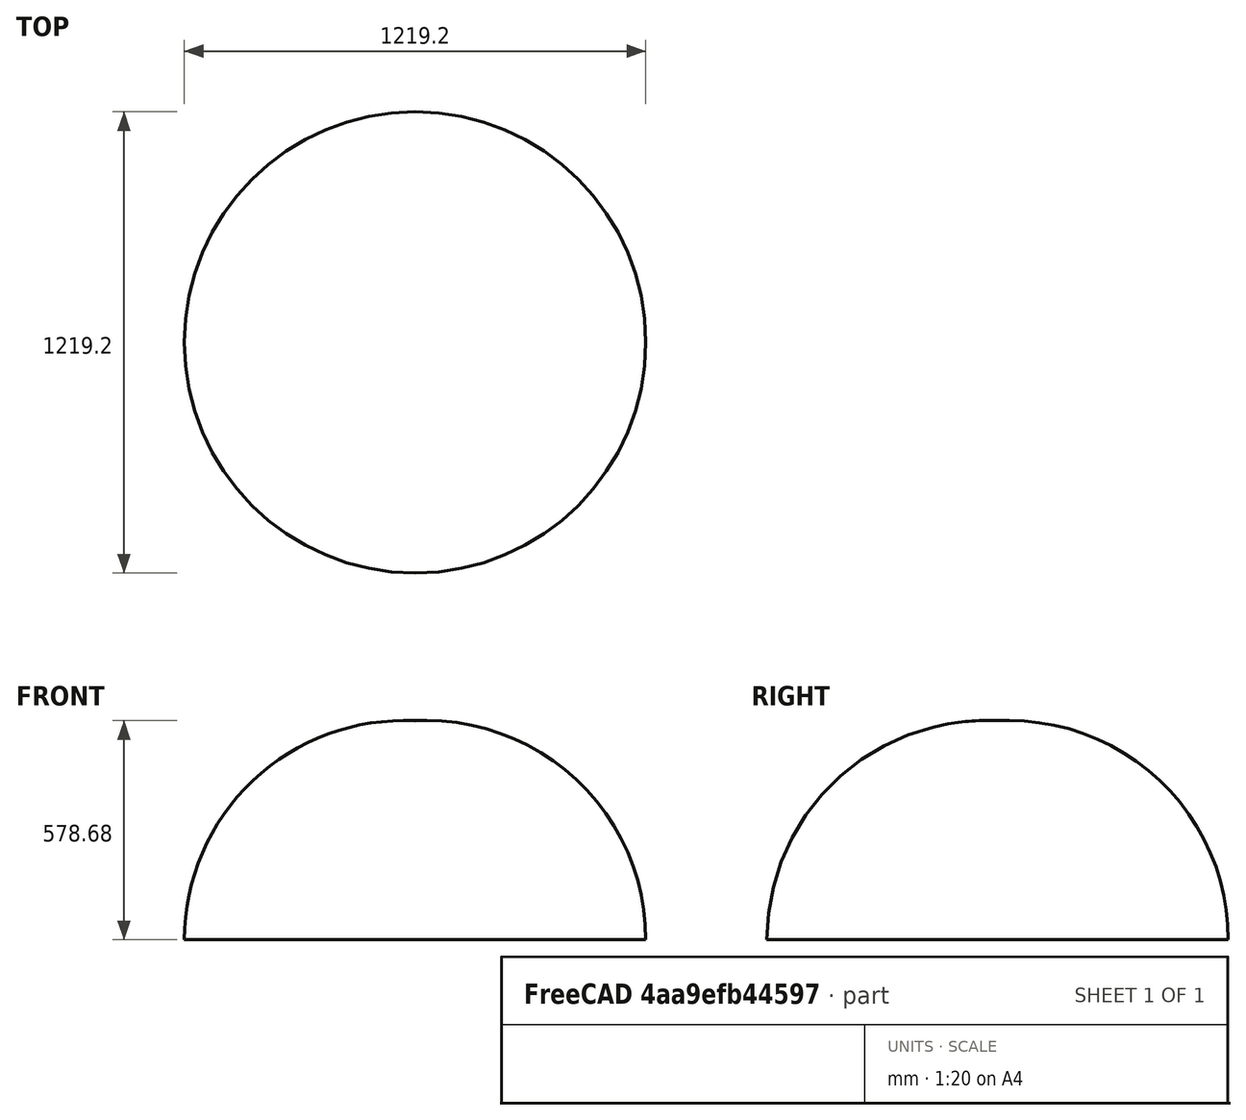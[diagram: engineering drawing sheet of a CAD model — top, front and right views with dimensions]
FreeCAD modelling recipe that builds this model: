
FCSTD DOCUMENT  (FreeCAD 0.20R29177 (Git))
Label: grass
License: All rights reserved
LicenseURL: http://en.wikipedia.org/wiki/All_rights_reserved
objects: Sketcher::SketchObject×1, PartDesign::Revolution×1, PartDesign::Body×1
note: 4 computed .brp shape members not serialized (recipe doc carries the construction recipe); baked Part::Feature solids carry a one-line shape summary decoded from their .brp

FEATURE [Sketcher::SketchObject] Sketch
  FullyConstrained = true
  MapMode = 5
  Placement = pos=(0,0,0) rot=(1,0,0;1.5708rad)
  Support = -> [XZ_Plane]
  sketch-geometry (3):
    g0: ArcOfCircle CenterX=-30.9232 CenterY=0 CenterZ=0 NormalX=0 NormalY=0 NormalZ=1 AngleXU=0 Radius=578.677 StartAngle=1.51733 EndAngle=3.14159
    g1: LineSegment StartX=-609.6 StartY=7.09e-14 StartZ=0 EndX=0 EndY=0 EndZ=0
    g2: LineSegment StartX=0 StartY=577.85 StartZ=0 EndX=0 EndY=0 EndZ=0
  constraints (9):
    c: PointOnObject(g0,g-1)
    c: PointOnObject(g0,g-2)
    c: PointOnObject(g0,g-1)
    c: DistanceX(g0,g-1) = 609.6
    c: Coincident(g1,g0)
    c: Coincident(g1,g-1)
    c: Coincident(g2,g0)
    c: Coincident(g2,g1)
    c: DistanceY(g1,g0) = 577.85
FEATURE [PartDesign::Revolution] Revolution
  Angle = 360
  Axis = (0,2e-16,1)
  Base = (0,0,0)
  Placement = pos=(0,0,0) rot=(1,0,0;1.5708rad)
  Profile = -> Sketch
  ReferenceAxis = -> Sketch [V_Axis]
FEATURE [PartDesign::Body] Body
  Group = -> [Sketch,Revolution]
  Origin = -> Origin
  Tip = -> Revolution
